# Revit family: Hager-Univers-IP54-D205-H800-Cl.II-Encl-NoHosted-CH-it
name_source: partatom
category: Electrical Equipment
units: mm (PartAtom-declared; Revit-internal decimal feet)

## family parameters
Always vertical = Yes
Cut with Voids When Loaded = No
Panel Configuration = Two Columns, Circuits Across
Part Type = Panelboard
Room Calculation Point = No
Round Connector Dimension = Use Diameter
Shared = No
Work Plane-Based = Yes

## types (4) — shared parameters
Default Elevation = 1219 mm
EF000003 - Tipo di montaggio = EV000384 - A parete
EF000007 - colore = EV000202 - bianco
EF000040 - Altezza = 800 mm  [stored 2.62467 ft]
EF000049 - profondità = 205 mm  [stored 0.672572 ft]
EF000116 - numero RAL = 9010
EF000118 - con piastra di montaggio = No
EF000266 - numero di file = 5
EF001088 - possibilità di applicazione = Yes
EF001596 - Attacco Lampada = EV000179 - acciaio
EF001613 - Integrità del circuito = EV000494 - senza
EF003532 - adatto per uso esterno = No
EF004293 - resistenza agli urti = EV006815 - IK09
EF005474 - grado di protezione (IP) = EV006419 - IP54
EF006244 - coperchio/porta trasparente = No
EF006306 - con serratura = No
EF007800 - adatto per parafulmine = No
EF008873 - corrente nominale (In) = 250 A
EF009170 - spessore materiale scatola = 1 mm  [stored 0.00328084 ft]
EF009171 - spessore materiale porta/coperchio = 1 mm  [stored 0.00328084 ft]
EF009212 - esecuzione coperchio = EV000116 - chiuso
EF015940 - Coprire con rilascio di sovrapressione = No
HG000002 - Con porta = Yes
HG000003 - Gamma = Univers
HG000006 - Ad incasso = No
HG000009 - Porta doppia a battente = No
HG000010 - Porte asimmetriche = No
HG000023 - Custodia a doppia sezione = No
HG000024 - Altezza della sezione inferiore = 600 mm
HG000026 - A pavimento = No
Manufacturer = Hager
Type Comments = Univers
zero-valued in all types: EF000218 - profondità di incasso, HG000027 - Altezza dello zoccolo

## per-type parameters (varying)
| type | EF000008 - Larghezza | EF000339 - tipo di copertura | EF000437 - numero di ingressi per conduttori | EF001131 - profondità interna | EF002950 - Numero moduli DIN | EF004427 - numero di moduli | EF004464 - tipo di porta | EF009554 - numero delle aperture per la piastra della flangia | HG000004 - Codice produttore |
| A parete IP54 L1050 A800 P205  - FP54QSW | 1050 mm | EV004216 - porta | 8 | 130 mm  [stored 0.426509 ft] | 48 | 240 | EV003602 - doppio | 8 | FP54QSW |
| A parete IP54 L300 A800 P205  - FP51QSW | 300 mm | EV001012 - coperchio | 2 | 130 mm  [stored 0.426509 ft] | 12 | 60 | EV002646 - singolo | 2 | FP51QSW |
| A parete IP54 L550 A800 P205  - FP52QSW | 550 mm | EV001012 - coperchio | 4 | 143 mm | 24 | 120 | EV002646 - singolo | 4 | FP52QSW |
| A parete IP54 L800 A800 P205  - FP53QSW | 800 mm  [stored 2.62467 ft] | EV001012 - coperchio | 6 | 143 mm | 36 | 180 | EV002646 - singolo | 6 | FP53QSW |

note: [stored X ft] marks values corroborated as IEEE doubles in the binary element streams (Revit-internal decimal feet)

## geometry (parser evidence)
native form markers: Blend x4, Sweep x11
no freeform markers — native parametric forms only
